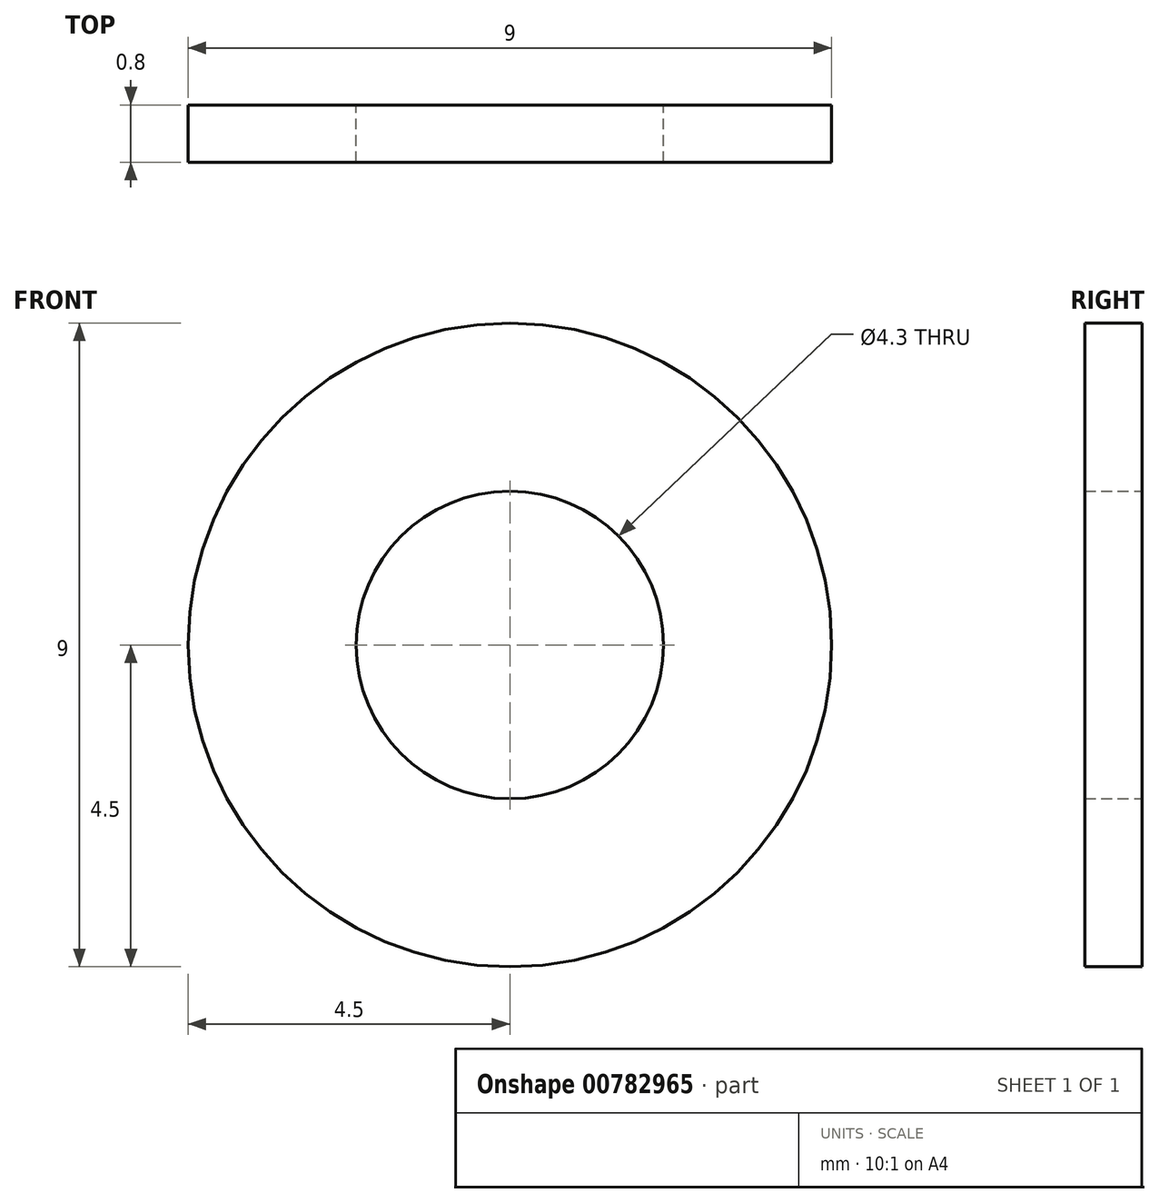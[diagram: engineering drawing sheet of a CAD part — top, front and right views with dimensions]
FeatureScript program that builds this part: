
annotation { "Feature Type Name" : "Feature", "Feature Type Description" : "" }
export const myFeature = defineFeature(function(context is Context, id is Id, definition is map)
    precondition{}
    {
        {
            var Q0;
            Q0=qCreatedBy(makeId("Front.planeOp"),FACE);
            var sketch = newSketch(context, id + "F0", { "sketchPlane" : qUnion([Q0])});
            skCircle(sketch, "E0", {"center": v(0, 0) * mm, "radius": 4.5 * mm});
            skCircle(sketch, "E1", {"center": v(0, 0) * mm, "radius": 2.15 * mm});
            skSolve(sketch);
        }
        {
            var Q0;
            Q0=qSketchRegion(id+"F0",true);
            extrude(context, id + "F1", {"entities" : qUnion([Q0]), "depth" : .8 * mm, "offsetDistance" : 25 * mm});
        }
    });
